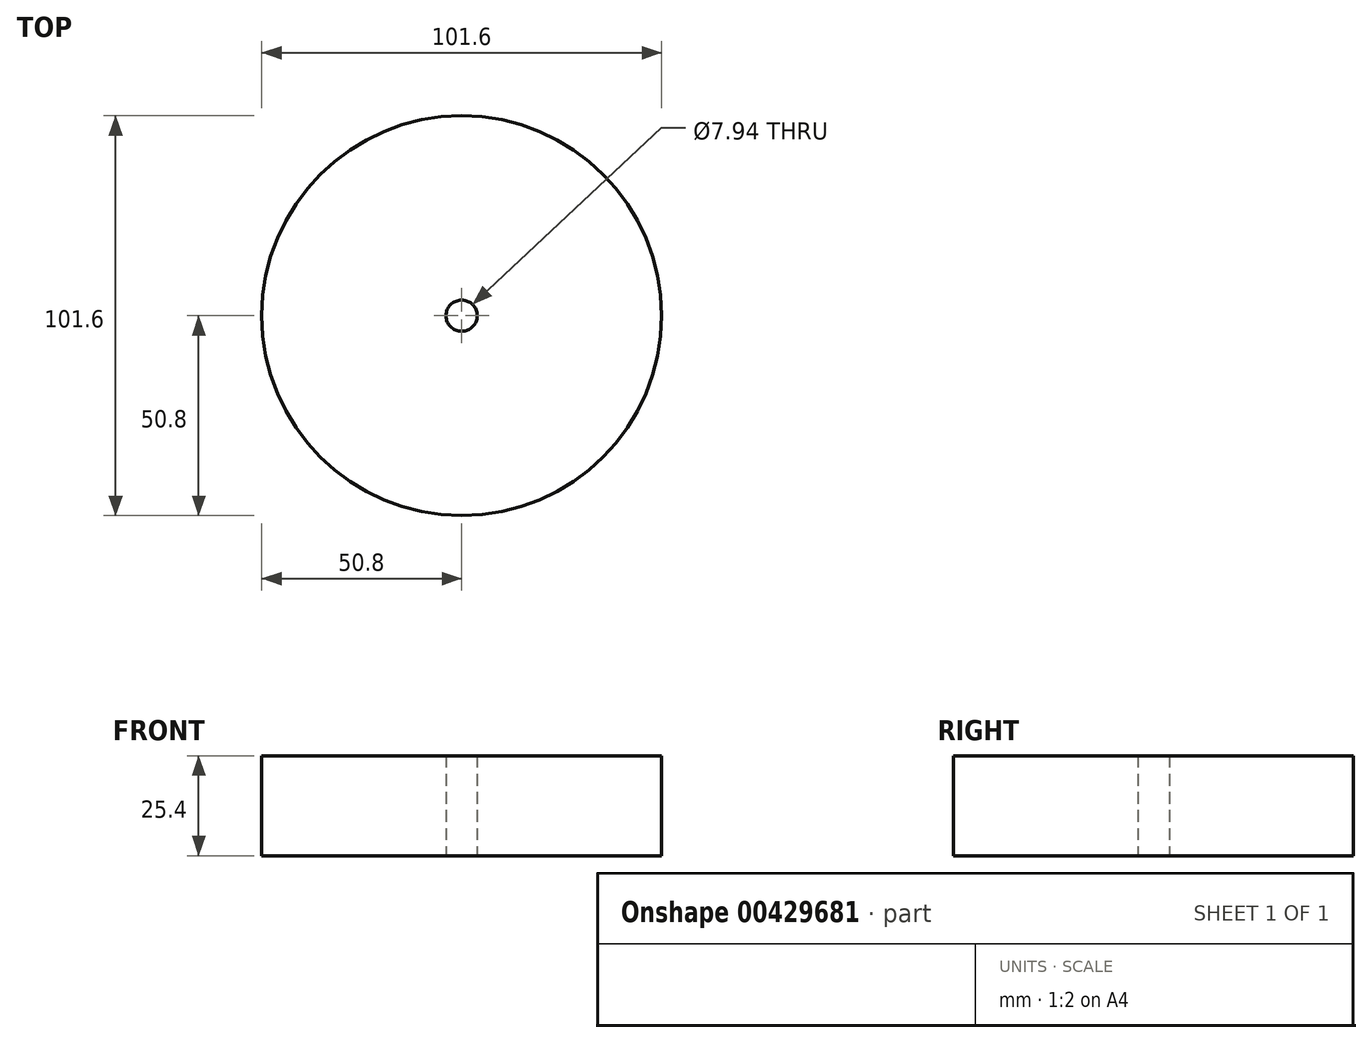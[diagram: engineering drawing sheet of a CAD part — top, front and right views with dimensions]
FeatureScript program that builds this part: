
annotation { "Feature Type Name" : "Feature", "Feature Type Description" : "" }
export const myFeature = defineFeature(function(context is Context, id is Id, definition is map)
    precondition{}
    {
        {
            var Q0;
            Q0=qCreatedBy(makeId("Top.planeOp"),FACE);
            var sketch = newSketch(context, id + "F0", { "sketchPlane" : qUnion([Q0])});
            skCircle(sketch, "E0", {"center": v(0, 0) * mm, "radius": 50.8 * mm});
            skCircle(sketch, "E1", {"center": v(0, 0) * mm, "radius": 3.97 * mm});
            skSolve(sketch);
        }
        {
            var Q0;
            Q0=makeQuery(id+"F0.imprint","IMPRINT",FACE,{"disambiguationData":[TD([[makeQuery(id+"F0.imprint","IMPRINT",EDGE,{"derivedFrom":sQuery(id+"F0.wireOp",EDGE,"E0")}),1.0]])]});
            extrude(context, id + "F1", {"entities" : qUnion([Q0]), "depth" : 25.4 * mm});
        }
    });
